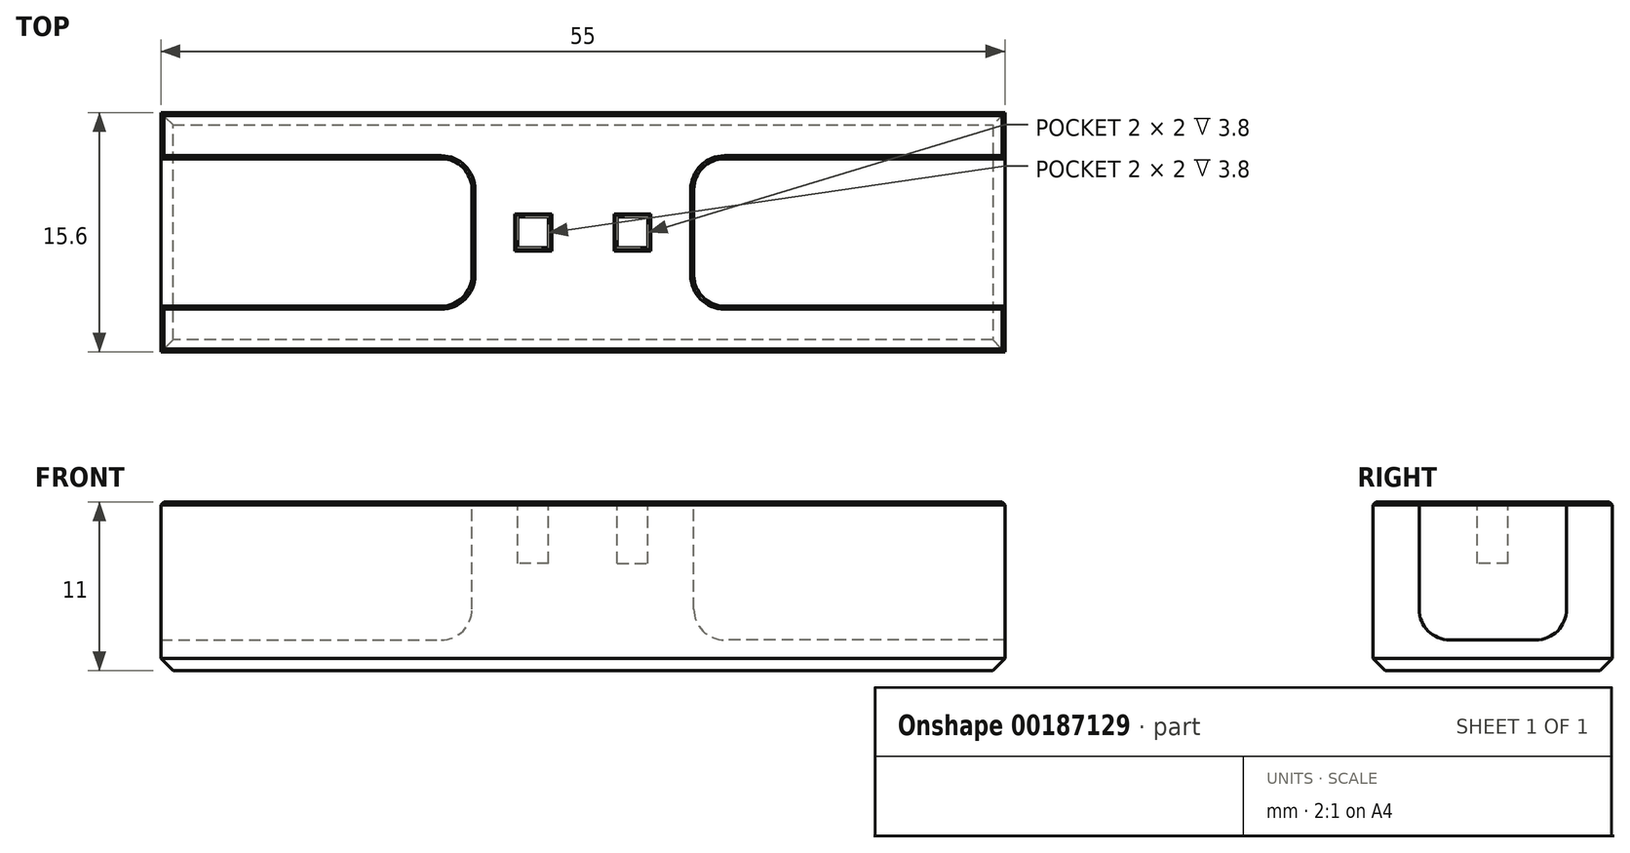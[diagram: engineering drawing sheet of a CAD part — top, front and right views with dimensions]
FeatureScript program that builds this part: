
annotation { "Feature Type Name" : "Feature", "Feature Type Description" : "" }
export const myFeature = defineFeature(function(context is Context, id is Id, definition is map)
    precondition{}
    {
        {
            var Q0;
            Q0=qCreatedBy(makeId("Top.planeOp"),FACE);
            var sketch = newSketch(context, id + "F0", { "sketchPlane" : qUnion([Q0])});
            skLineSegment(sketch, "E0.rect.bottom", {"start": v(27.5, 7.8) * mm, "end": v(-27.5, 7.8) * mm});
            skLineSegment(sketch, "E0.rect.top", {"start": v(27.5, -7.8) * mm, "end": v(-27.5, -7.8) * mm});
            skLineSegment(sketch, "E0.rect.left", {"start": v(27.5, 7.8) * mm, "end": v(27.5, -7.8) * mm});
            skLineSegment(sketch, "E0.rect.right", {"start": v(-27.5, 7.8) * mm, "end": v(-27.5, -7.8) * mm});
            skPoint(sketch, "E0.rect.middle", {"position": v(0, 0) * mm});
            skSolve(sketch);
        }
        {
            var Q0;
            Q0=qSketchRegion(id+"F0",true);
            extrude(context, id + "F1", {"entities" : qUnion([Q0]), "depth" : 11 * mm});
        }
        {
            var Q0;
            Q0=makeQuery(id+"F1.opExtrude","CAP_FACE",FACE,{"disambiguationData":[OSD([sQuery(id+"F0.wireOp",EDGE,"E0.rect.bottom"),sQuery(id+"F0.wireOp",EDGE,"E0.rect.top"),sQuery(id+"F0.wireOp",EDGE,"E0.rect.left"),sQuery(id+"F0.wireOp",EDGE,"E0.rect.right")])],"isStart":false});
            var sketch = newSketch(context, id + "F2", { "sketchPlane" : qUnion([Q0])});
            skLineSegment(sketch, "E1", {"start": v(-27.5, 0) * mm, "end": v(27.5, 0) * mm, "construction": true});
            skLineSegment(sketch, "E2", {"start": v(0, 7.8) * mm, "end": v(0, -7.8) * mm, "construction": true});
            skLineSegment(sketch, "E3.rect.bottom", {"start": v(-2.23, 1) * mm, "end": v(-4.23, 1) * mm});
            skLineSegment(sketch, "E3.rect.top", {"start": v(-2.23, -1) * mm, "end": v(-4.23, -1) * mm});
            skLineSegment(sketch, "E3.rect.left", {"start": v(-2.23, 1) * mm, "end": v(-2.23, -1) * mm});
            skLineSegment(sketch, "E3.rect.right", {"start": v(-4.23, 1) * mm, "end": v(-4.23, -1) * mm});
            skPoint(sketch, "E3.rect.middle", {"position": v(-3.23, 0) * mm});
            skLineSegment(sketch, "E4.MirrorCS", {"start": v(2.23, 1) * mm, "end": v(4.23, 1) * mm});
            skPoint(sketch, "E5.MirrorP", {"position": v(3.23, 0) * mm});
            skLineSegment(sketch, "E6.MirrorCS", {"start": v(4.23, 1) * mm, "end": v(4.23, -1) * mm});
            skLineSegment(sketch, "E7.MirrorCS", {"start": v(2.23, 1) * mm, "end": v(2.23, -1) * mm});
            skLineSegment(sketch, "E8.MirrorCS", {"start": v(2.23, -1) * mm, "end": v(4.23, -1) * mm});
            skSolve(sketch);
        }
        {
            var Q0;
            Q0=qSketchRegion(id+"F2",true);
            var Q1;
            Q1=makeQuery(id+"FmLzmjlziKLHTuf_1.boolean.opBoolean","COPY",FACE,{"derivedFrom":makeQuery(id+"FmLzmjlziKLHTuf_1.opExtrude","CAP_FACE",FACE,{"disambiguationData":[OSD([sQuery(id+"F9PTREojc0uJMFG_1.wireOp",EDGE,"231e34c2-eba5-454b-9980-f65723292a92")])],"isStart":false})});
            extrude(context, id + "F3", {"entities" : qUnion([Q0]), "operationType" : NewBodyOperationType.REMOVE, "oppositeDirection" : true, "endBoundEntityFace" : qUnion([Q1]), "depth" : 4 * mm});
        }
        {
            var Q0;
            Q0=makeQuery(id+"F1.opExtrude","CAP_FACE",FACE,{"disambiguationData":[OSD([sQuery(id+"F0.wireOp",EDGE,"E0.rect.bottom"),sQuery(id+"F0.wireOp",EDGE,"E0.rect.top"),sQuery(id+"F0.wireOp",EDGE,"E0.rect.left"),sQuery(id+"F0.wireOp",EDGE,"E0.rect.right")])],"isStart":false});
            var sketch = newSketch(context, id + "F4", { "sketchPlane" : qUnion([Q0])});
            skLineSegment(sketch, "E9", {"start": v(-27.5, 0) * mm, "end": v(27.5, 0) * mm, "construction": true});
            skLineSegment(sketch, "E10", {"start": v(0, 7.8) * mm, "end": v(0, -7.8) * mm, "construction": true});
            skLineSegment(sketch, "E11.rect.bottom", {"start": v(-27.5, 4.8) * mm, "end": v(-7.23, 4.8) * mm});
            skLineSegment(sketch, "E11.rect.top", {"start": v(-27.5, -4.8) * mm, "end": v(-7.23, -4.8) * mm});
            skLineSegment(sketch, "E11.rect.left", {"start": v(-27.5, 4.8) * mm, "end": v(-27.5, -4.8) * mm});
            skLineSegment(sketch, "E11.rect.right", {"start": v(-7.23, 4.8) * mm, "end": v(-7.23, -4.8) * mm});
            skPoint(sketch, "E11.rect.middle", {"position": v(-17.36, 0) * mm});
            skLineSegment(sketch, "E12.MirrorCS", {"start": v(27.5, 4.8) * mm, "end": v(7.23, 4.8) * mm});
            skLineSegment(sketch, "E13.MirrorCS", {"start": v(27.5, -4.8) * mm, "end": v(7.23, -4.8) * mm});
            skLineSegment(sketch, "E14.MirrorCS", {"start": v(7.23, 4.8) * mm, "end": v(7.23, -4.8) * mm});
            skLineSegment(sketch, "E15.MirrorCS", {"start": v(27.5, 4.8) * mm, "end": v(27.5, -4.8) * mm});
            skPoint(sketch, "E16.MirrorP", {"position": v(17.36, 0) * mm});
            skSolve(sketch);
        }
        {
            var Q0;
            Q0=qSketchRegion(id+"F4",true);
            extrude(context, id + "F5", {"entities" : qUnion([Q0]), "operationType" : NewBodyOperationType.REMOVE, "oppositeDirection" : true, "depth" : 9 * mm});
        }
        {
            var Q0;
            Q0=makeQuery(id+"F5.boolean.opBoolean","COPY",EDGE,{"derivedFrom":makeQuery(id+"F5.opExtrude","SWEPT_EDGE",EDGE,{"disambiguationData":[OSD([sQuery(id+"F4.wireOp",EDGE,"E11.rect.bottom"),sQuery(id+"F4.wireOp",EDGE,"E11.rect.right")])]})});
            var Q1;
            Q1=makeQuery(id+"F5.boolean.opBoolean","COPY",EDGE,{"derivedFrom":makeQuery(id+"F5.opExtrude","CAP_EDGE",EDGE,{"disambiguationData":[OSD([sQuery(id+"F4.wireOp",EDGE,"E11.rect.bottom")])],"isStart":false})});
            var Q2;
            Q2=makeQuery(id+"F5.boolean.opBoolean","COPY",EDGE,{"derivedFrom":makeQuery(id+"F5.opExtrude","CAP_EDGE",EDGE,{"disambiguationData":[OSD([sQuery(id+"F4.wireOp",EDGE,"E11.rect.right")])],"isStart":false})});
            var Q3;
            Q3=makeQuery(id+"F5.boolean.opBoolean","COPY",EDGE,{"derivedFrom":makeQuery(id+"F5.opExtrude","CAP_EDGE",EDGE,{"disambiguationData":[OSD([sQuery(id+"F4.wireOp",EDGE,"E11.rect.top")])],"isStart":false})});
            var Q4;
            Q4=makeQuery(id+"F5.boolean.opBoolean","COPY",EDGE,{"derivedFrom":makeQuery(id+"F5.opExtrude","SWEPT_EDGE",EDGE,{"disambiguationData":[OSD([sQuery(id+"F4.wireOp",EDGE,"E11.rect.top"),sQuery(id+"F4.wireOp",EDGE,"E11.rect.right")])]})});
            var Q5;
            Q5=makeQuery(id+"F5.boolean.opBoolean","COPY",EDGE,{"derivedFrom":makeQuery(id+"F5.opExtrude","CAP_EDGE",EDGE,{"disambiguationData":[OSD([sQuery(id+"F4.wireOp",EDGE,"E14.MirrorCS")])],"isStart":false})});
            var Q6;
            Q6=makeQuery(id+"F5.boolean.opBoolean","COPY",EDGE,{"derivedFrom":makeQuery(id+"F5.opExtrude","SWEPT_EDGE",EDGE,{"disambiguationData":[OSD([sQuery(id+"F4.wireOp",EDGE,"E12.MirrorCS"),sQuery(id+"F4.wireOp",EDGE,"E14.MirrorCS")])]})});
            var Q7;
            Q7=makeQuery(id+"F5.boolean.opBoolean","COPY",EDGE,{"derivedFrom":makeQuery(id+"F5.opExtrude","CAP_EDGE",EDGE,{"disambiguationData":[OSD([sQuery(id+"F4.wireOp",EDGE,"E12.MirrorCS")])],"isStart":false})});
            var Q8;
            Q8=makeQuery(id+"F5.boolean.opBoolean","COPY",EDGE,{"derivedFrom":makeQuery(id+"F5.opExtrude","CAP_EDGE",EDGE,{"disambiguationData":[OSD([sQuery(id+"F4.wireOp",EDGE,"E13.MirrorCS")])],"isStart":false})});
            var Q9;
            Q9=makeQuery(id+"F5.boolean.opBoolean","COPY",EDGE,{"derivedFrom":makeQuery(id+"F5.opExtrude","SWEPT_EDGE",EDGE,{"disambiguationData":[OSD([sQuery(id+"F4.wireOp",EDGE,"E13.MirrorCS"),sQuery(id+"F4.wireOp",EDGE,"E14.MirrorCS")])]})});
            fillet(context, id + "F6", {"entities" : qUnion([Q0, Q1, Q2, Q3, Q4, Q5, Q6, Q7, Q8, Q9]), "radius" : 2 * mm, "tangentPropagation" : true, "allowEdgeOverflow" : false});
        }
        {
            var Q0;
            Q0=makeQuery(id+"F1.opExtrude","CAP_FACE",FACE,{"disambiguationData":[OSD([sQuery(id+"F0.wireOp",EDGE,"E0.rect.bottom"),sQuery(id+"F0.wireOp",EDGE,"E0.rect.top"),sQuery(id+"F0.wireOp",EDGE,"E0.rect.left"),sQuery(id+"F0.wireOp",EDGE,"E0.rect.right")])],"isStart":false});
            chamfer(context, id + "F7", {"entities" : qUnion([Q0]), "width" : 0.2 * mm, "tangentPropagation" : true});
        }
        {
            var Q0;
            Q0=makeQuery(id+"F1.opExtrude","CAP_FACE",FACE,{"disambiguationData":[OSD([sQuery(id+"F0.wireOp",EDGE,"E0.rect.bottom"),sQuery(id+"F0.wireOp",EDGE,"E0.rect.top"),sQuery(id+"F0.wireOp",EDGE,"E0.rect.left"),sQuery(id+"F0.wireOp",EDGE,"E0.rect.right")])],"isStart":true});
            chamfer(context, id + "F8", {"entities" : qUnion([Q0]), "width" : 0.8 * mm, "tangentPropagation" : true});
        }
    });
